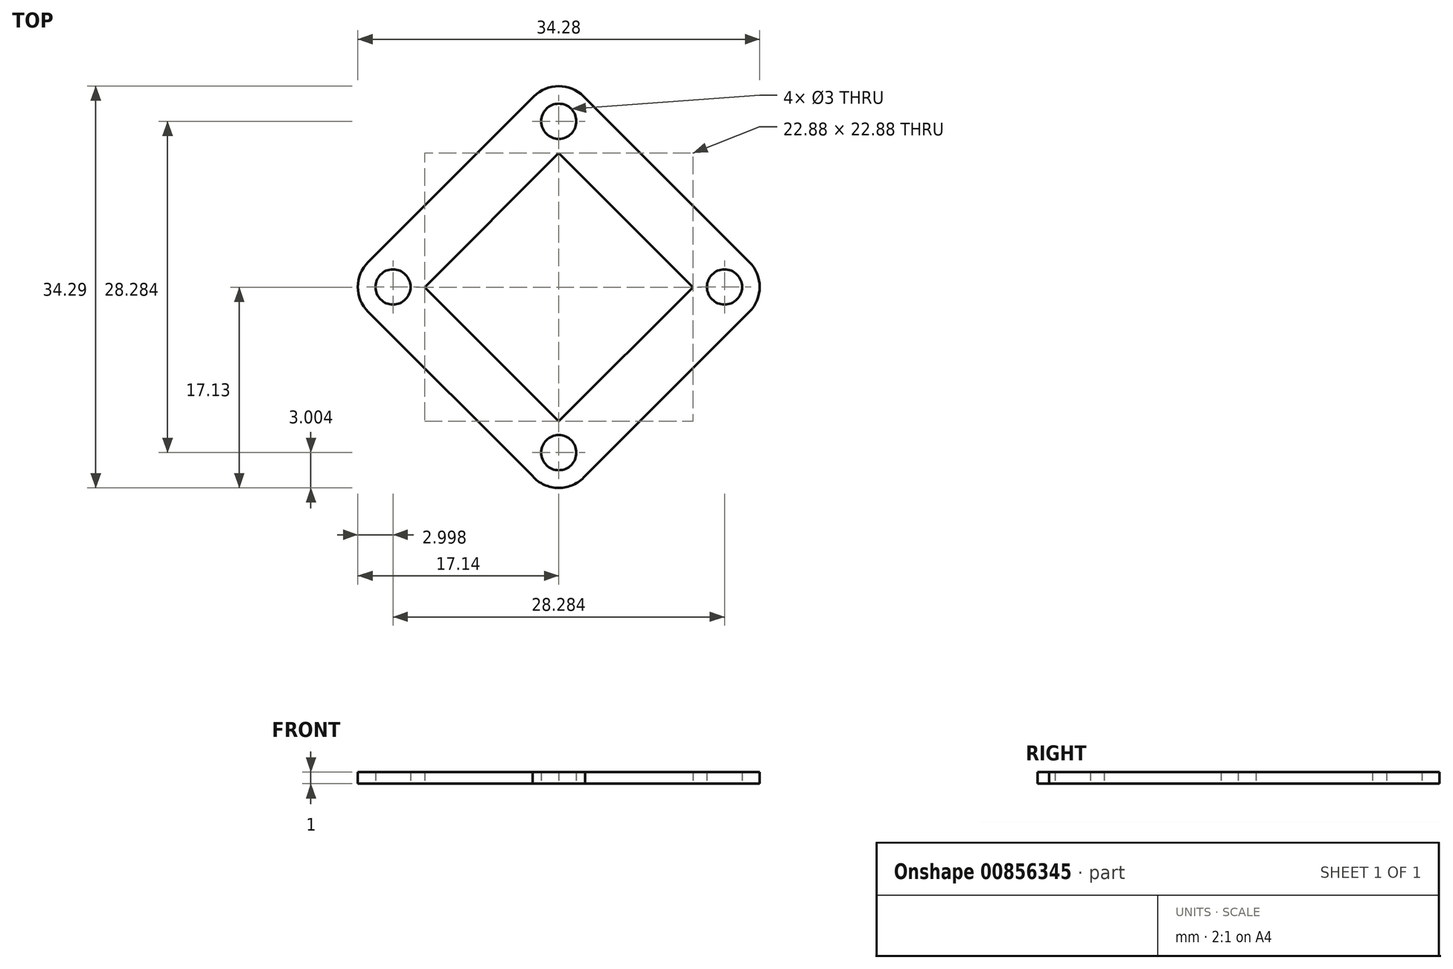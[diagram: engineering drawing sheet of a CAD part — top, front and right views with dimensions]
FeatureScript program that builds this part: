
annotation { "Feature Type Name" : "Feature", "Feature Type Description" : "" }
export const myFeature = defineFeature(function(context is Context, id is Id, definition is map)
    precondition{}
    {
        {
            var Q0;
            Q0=qCreatedBy(makeId("Top.planeOp"),FACE);
            var sketch = newSketch(context, id + "F0", { "sketchPlane" : qUnion([Q0])});
            skCircle(sketch, "E0.0", {"center": v(0, -14.13) * mm, "radius": 1.5 * mm});
            skCircle(sketch, "E1.0", {"center": v(0, 14.16) * mm, "radius": 1.5 * mm});
            skCircle(sketch, "E2.0", {"center": v(14.14, 0.02) * mm, "radius": 1.5 * mm});
            skPoint(sketch, "E3.0", {"position": v(-14.14, 0.02) * mm});
            skCircle(sketch, "E4.0", {"center": v(-14.14, 0.02) * mm, "radius": 1.5 * mm});
            skLineSegment(sketch, "E5", {"start": v(-2.12, -16.25) * mm, "end": v(-16.26, -2.1) * mm});
            skLineSegment(sketch, "E6", {"start": v(-16.26, 2.14) * mm, "end": v(-2.12, 16.28) * mm});
            skLineSegment(sketch, "E7", {"start": v(2.12, 16.28) * mm, "end": v(16.26, 2.14) * mm});
            skLineSegment(sketch, "E8", {"start": v(16.26, -2.1) * mm, "end": v(2.25, -16.12) * mm});
            skArc(sketch, "E9", {"start": v(2.25, -16.12) * mm, "mid": v(0, -17.13) * mm, "end": v(-2.24, -16.12) * mm});
            skArc(sketch, "E10", {"start": v(-16.26, -2.1) * mm, "mid": v(-17.14, 0.02) * mm, "end": v(-16.26, 2.14) * mm});
            skArc(sketch, "E11", {"start": v(-2.12, 16.28) * mm, "mid": v(0, 17.16) * mm, "end": v(2.12, 16.28) * mm});
            skArc(sketch, "E12", {"start": v(16.26, 2.14) * mm, "mid": v(17.14, 0.02) * mm, "end": v(16.26, -2.1) * mm});
            skLineSegment(sketch, "E13", {"start": v(0, 11.44) * mm, "end": v(-11.44, 0) * mm});
            skLineSegment(sketch, "E14", {"start": v(-11.44, 0) * mm, "end": v(0, -11.44) * mm});
            skLineSegment(sketch, "E15", {"start": v(0, -11.44) * mm, "end": v(11.44, 0) * mm});
            skLineSegment(sketch, "E16", {"start": v(11.44, 0) * mm, "end": v(0, 11.44) * mm});
            skSolve(sketch);
        }
        {
            var Q0;
            Q0 = qSketchRegion(id + "F0", true);
            extrude(context, id + "F1", {"entities" : qUnion([Q0]), "depth" : 1 * mm, "offsetDistance" : 25 * mm});
        }
    });
